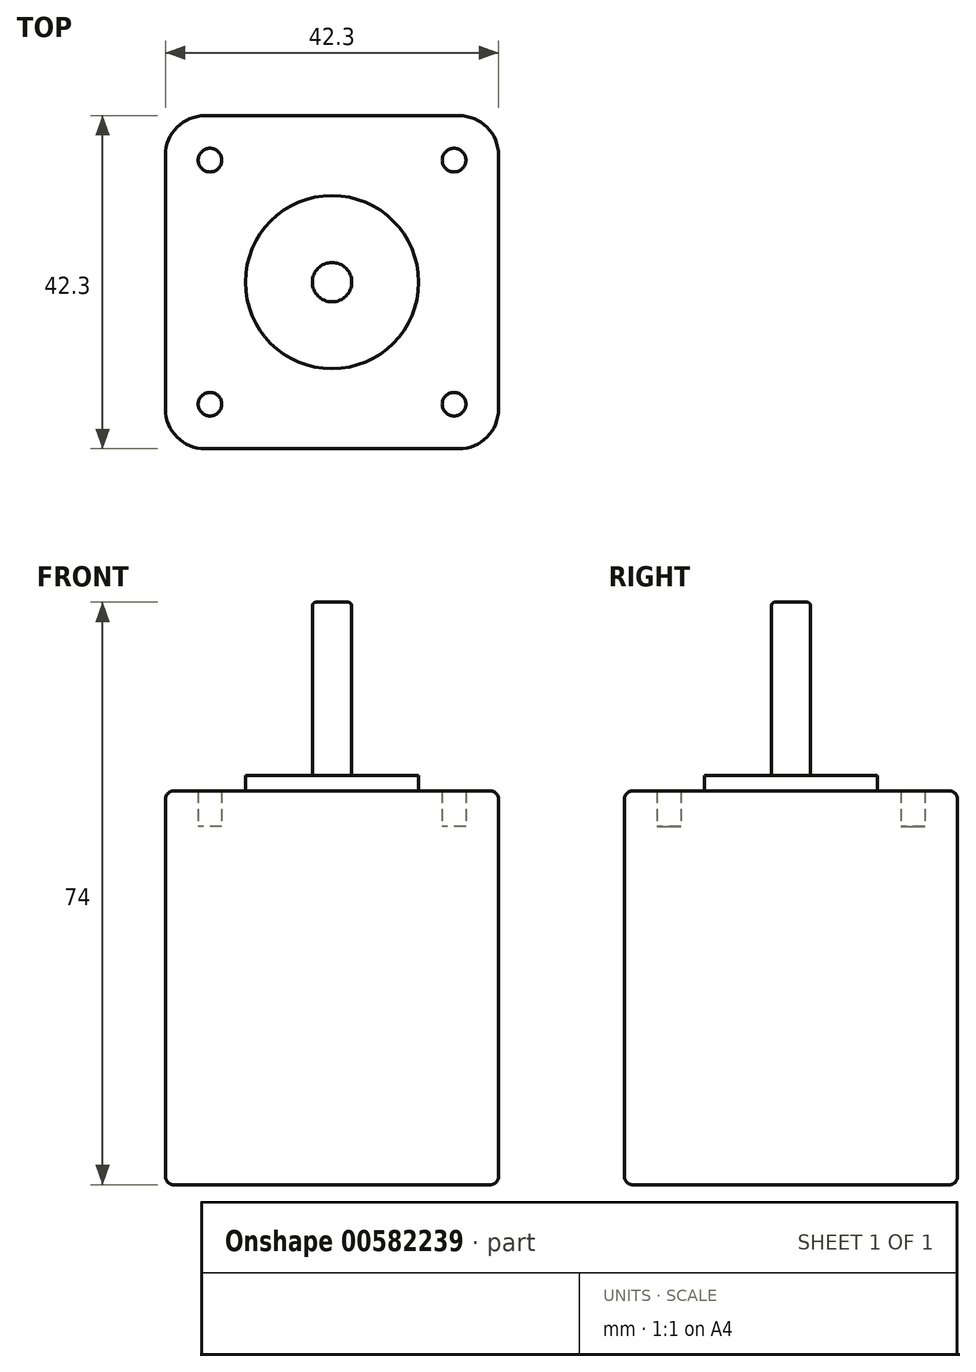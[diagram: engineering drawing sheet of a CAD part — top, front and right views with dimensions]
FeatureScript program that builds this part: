
annotation { "Feature Type Name" : "Feature", "Feature Type Description" : "" }
export const myFeature = defineFeature(function(context is Context, id is Id, definition is map)
    precondition{}
    {
        {
            assignVariable(context, id + "F0", {"name" : "Height", "anyValue" : 50});
        }
        {
            var Q0;
            Q0=qCreatedBy(makeId("Top.planeOp"),FACE);
            var sketch = newSketch(context, id + "F1", { "sketchPlane" : qUnion([Q0])});
            skLineSegment(sketch, "E0.bottom", {"start": v(-21.15, 21.15) * mm, "end": v(21.15, 21.15) * mm});
            skLineSegment(sketch, "E0.top", {"start": v(-21.15, -21.15) * mm, "end": v(21.15, -21.15) * mm});
            skLineSegment(sketch, "E0.left", {"start": v(-21.15, 21.15) * mm, "end": v(-21.15, -21.15) * mm});
            skLineSegment(sketch, "E0.right", {"start": v(21.15, 21.15) * mm, "end": v(21.15, -21.15) * mm});
            skLineSegment(sketch, "E1.bottom", {"start": v(-15.5, 15.5) * mm, "end": v(15.5, 15.5) * mm, "construction": true});
            skLineSegment(sketch, "E1.top", {"start": v(-15.5, -15.5) * mm, "end": v(15.5, -15.5) * mm, "construction": true});
            skLineSegment(sketch, "E1.left", {"start": v(-15.5, 15.5) * mm, "end": v(-15.5, -15.5) * mm, "construction": true});
            skLineSegment(sketch, "E1.right", {"start": v(15.5, 15.5) * mm, "end": v(15.5, -15.5) * mm, "construction": true});
            skCircle(sketch, "E2", {"center": v(-15.5, 15.5) * mm, "radius": 1.5 * mm});
            skCircle(sketch, "E3", {"center": v(15.5, 15.5) * mm, "radius": 1.5 * mm});
            skCircle(sketch, "E4", {"center": v(15.5, -15.5) * mm, "radius": 1.5 * mm});
            skCircle(sketch, "E5", {"center": v(-15.5, -15.5) * mm, "radius": 1.5 * mm});
            skCircle(sketch, "E6", {"center": v(0, 0) * mm, "radius": 11 * mm});
            skCircle(sketch, "E7", {"center": v(0, 0) * mm, "radius": 2.5 * mm});
            skSolve(sketch);
        }
        {
            var Q0;
            Q0=makeQuery(id+"F1.imprint","IMPRINT",FACE,{"disambiguationData":[TD([[makeQuery(id+"F1.imprint","IMPRINT",EDGE,{"derivedFrom":sQuery(id+"F1.wireOp",EDGE,"E2")}),1.0]])]});
            var Q1;
            Q1=makeQuery(id+"F1.imprint","IMPRINT",FACE,{"disambiguationData":[TD([[makeQuery(id+"F1.imprint","IMPRINT",EDGE,{"derivedFrom":sQuery(id+"F1.wireOp",EDGE,"E5")}),1.0]])]});
            var Q2;
            Q2=makeQuery(id+"F1.imprint","IMPRINT",FACE,{"disambiguationData":[TD([[makeQuery(id+"F1.imprint","IMPRINT",EDGE,{"derivedFrom":sQuery(id+"F1.wireOp",EDGE,"E4")}),1.0]])]});
            var Q3;
            Q3=makeQuery(id+"F1.imprint","IMPRINT",FACE,{"disambiguationData":[TD([[makeQuery(id+"F1.imprint","IMPRINT",EDGE,{"derivedFrom":sQuery(id+"F1.wireOp",EDGE,"E3")}),1.0]])]});
            var Q4;
            Q4=makeQuery(id+"F1.imprint","IMPRINT",FACE,{"disambiguationData":[TD([[makeQuery(id+"F1.imprint","IMPRINT",EDGE,{"derivedFrom":sQuery(id+"F1.wireOp",EDGE,"E0.bottom")}),-1.0]])]});
            var Q5;
            Q5=makeQuery(id+"F1.imprint","IMPRINT",FACE,{"disambiguationData":[TD([[makeQuery(id+"F1.imprint","IMPRINT",EDGE,{"derivedFrom":sQuery(id+"F1.wireOp",EDGE,"E6")}),1.0]])]});
            var Q6;
            Q6=makeQuery(id+"F1.imprint","IMPRINT",FACE,{"disambiguationData":[TD([[makeQuery(id+"F1.imprint","IMPRINT",EDGE,{"derivedFrom":sQuery(id+"F1.wireOp",EDGE,"E7")}),1.0]])]});
            extrude(context, id + "F2", {"entities" : qUnion([Q0, Q1, Q2, Q3, Q4, Q5, Q6]), "depth" : (getVariable(context, 'Height') - 4.5) * mm, "offsetDistance" : 25 * mm});
        }
        {
            var Q0;
            Q0=makeQuery(id+"F1.imprint","IMPRINT",FACE,{"disambiguationData":[TD([[makeQuery(id+"F1.imprint","IMPRINT",EDGE,{"derivedFrom":sQuery(id+"F1.wireOp",EDGE,"E0.bottom")}),-1.0]])]});
            var Q1;
            Q1=makeQuery(id+"F1.imprint","IMPRINT",FACE,{"disambiguationData":[TD([[makeQuery(id+"F1.imprint","IMPRINT",EDGE,{"derivedFrom":sQuery(id+"F1.wireOp",EDGE,"E6")}),1.0]])]});
            var Q2;
            Q2=makeQuery(id+"F1.imprint","IMPRINT",FACE,{"disambiguationData":[TD([[makeQuery(id+"F1.imprint","IMPRINT",EDGE,{"derivedFrom":sQuery(id+"F1.wireOp",EDGE,"E7")}),1.0]])]});
            extrude(context, id + "F3", {"entities" : qUnion([Q0, Q1, Q2]), "operationType" : NewBodyOperationType.ADD, "depth" : (getVariable(context, 'Height')) * mm, "offsetDistance" : 25 * mm, "hasSecondDirection" : true, "secondDirectionOppositeDirection" : false, "secondDirectionDepth" : (getVariable(context, 'Height') - 4.5) * mm});
        }
        {
            var Q0;
            Q0=makeQuery(id+"F1.imprint","IMPRINT",FACE,{"disambiguationData":[TD([[makeQuery(id+"F1.imprint","IMPRINT",EDGE,{"derivedFrom":sQuery(id+"F1.wireOp",EDGE,"E6")}),1.0]])]});
            var Q1;
            Q1=makeQuery(id+"F1.imprint","IMPRINT",FACE,{"disambiguationData":[TD([[makeQuery(id+"F1.imprint","IMPRINT",EDGE,{"derivedFrom":sQuery(id+"F1.wireOp",EDGE,"E7")}),1.0]])]});
            extrude(context, id + "F4", {"entities" : qUnion([Q0, Q1]), "operationType" : NewBodyOperationType.ADD, "depth" : (getVariable(context, 'Height') + 2) * mm, "offsetDistance" : 25 * mm, "hasSecondDirection" : true, "secondDirectionOppositeDirection" : false, "secondDirectionDepth" : (getVariable(context, 'Height')) * mm});
        }
        {
            var Q0;
            Q0=makeQuery(id+"F1.imprint","IMPRINT",FACE,{"disambiguationData":[TD([[makeQuery(id+"F1.imprint","IMPRINT",EDGE,{"derivedFrom":sQuery(id+"F1.wireOp",EDGE,"E7")}),1.0]])]});
            extrude(context, id + "F5", {"entities" : qUnion([Q0]), "operationType" : NewBodyOperationType.ADD, "depth" : (getVariable(context, 'Height') + 24) * mm, "offsetDistance" : 25 * mm, "hasSecondDirection" : true, "secondDirectionOppositeDirection" : false, "secondDirectionDepth" : (getVariable(context, 'Height') + 2) * mm});
        }
        {
            var Q0;
            Q0=makeQuery(id+"F5.opExtrude","CAP_EDGE",EDGE,{"disambiguationData":[OSD([sQuery(id+"F1.wireOp",EDGE,"E7")])],"isStart":false});
            fillet(context, id + "F6", {"entities" : qUnion([Q0]), "radius" : 0.5 * mm, "tangentPropagation" : true, "allowEdgeOverflow" : false});
        }
        {
            var Q0;
            {var subQ0=sQuery(id+"F1.wireOp",EDGE,"E0.left");var subQ1=sQuery(id+"F1.wireOp",EDGE,"E0.top");Q0=makeQuery(id+"F3.boolean.opBoolean","MERGE",EDGE,{"derivedFrom":[makeQuery(id+"F2.opExtrude","SWEPT_EDGE",EDGE,{"disambiguationData":[OSD([subQ1,subQ0])]}),makeQuery(id+"F3.opExtrude","SWEPT_EDGE",EDGE,{"disambiguationData":[OSD([subQ1,subQ0])]})]});}
            var Q1;
            {var subQ0=sQuery(id+"F1.wireOp",EDGE,"E0.left");var subQ1=sQuery(id+"F1.wireOp",EDGE,"E0.bottom");Q1=makeQuery(id+"F3.boolean.opBoolean","MERGE",EDGE,{"derivedFrom":[makeQuery(id+"F2.opExtrude","SWEPT_EDGE",EDGE,{"disambiguationData":[OSD([subQ1,subQ0])]}),makeQuery(id+"F3.opExtrude","SWEPT_EDGE",EDGE,{"disambiguationData":[OSD([subQ1,subQ0])]})]});}
            var Q2;
            {var subQ0=sQuery(id+"F1.wireOp",EDGE,"E0.right");var subQ1=sQuery(id+"F1.wireOp",EDGE,"E0.bottom");Q2=makeQuery(id+"F3.boolean.opBoolean","MERGE",EDGE,{"derivedFrom":[makeQuery(id+"F2.opExtrude","SWEPT_EDGE",EDGE,{"disambiguationData":[OSD([subQ1,subQ0])]}),makeQuery(id+"F3.opExtrude","SWEPT_EDGE",EDGE,{"disambiguationData":[OSD([subQ1,subQ0])]})]});}
            var Q3;
            {var subQ0=sQuery(id+"F1.wireOp",EDGE,"E0.right");var subQ1=sQuery(id+"F1.wireOp",EDGE,"E0.top");Q3=makeQuery(id+"F3.boolean.opBoolean","MERGE",EDGE,{"derivedFrom":[makeQuery(id+"F2.opExtrude","SWEPT_EDGE",EDGE,{"disambiguationData":[OSD([subQ1,subQ0])]}),makeQuery(id+"F3.opExtrude","SWEPT_EDGE",EDGE,{"disambiguationData":[OSD([subQ1,subQ0])]})]});}
            fillet(context, id + "F7", {"entities" : qUnion([Q0, Q1, Q2, Q3]), "radius" : 5 * mm, "tangentPropagation" : true, "allowEdgeOverflow" : false});
        }
        {
            var Q0;
            {var subQ0=sQuery(id+"F1.wireOp",EDGE,"E0.left");var subQ1=sQuery(id+"F1.wireOp",EDGE,"E0.bottom");Q0=makeQuery(id+"F7.opFillet","BLEND_EDGE",EDGE,{"blendedFrom":[makeQuery(id+"F3.boolean.opBoolean","MERGE",EDGE,{"derivedFrom":[makeQuery(id+"F2.opExtrude","SWEPT_EDGE",EDGE,{"disambiguationData":[OSD([subQ1,subQ0])]}),makeQuery(id+"F3.opExtrude","SWEPT_EDGE",EDGE,{"disambiguationData":[OSD([subQ1,subQ0])]})]}),makeQuery(id+"F3.opExtrude","CAP_FACE",FACE,{"disambiguationData":[OSD([subQ1,sQuery(id+"F1.wireOp",EDGE,"E0.top"),subQ0,sQuery(id+"F1.wireOp",EDGE,"E0.right"),sQuery(id+"F1.wireOp",EDGE,"E2"),sQuery(id+"F1.wireOp",EDGE,"E3"),sQuery(id+"F1.wireOp",EDGE,"E4"),sQuery(id+"F1.wireOp",EDGE,"E5")])],"isStart":false})],"blendedInto":[makeQuery(id+"F3.opExtrude","CAP_FACE",FACE,{"disambiguationData":[OSD([subQ1,sQuery(id+"F1.wireOp",EDGE,"E0.top"),subQ0,sQuery(id+"F1.wireOp",EDGE,"E0.right"),sQuery(id+"F1.wireOp",EDGE,"E2"),sQuery(id+"F1.wireOp",EDGE,"E3"),sQuery(id+"F1.wireOp",EDGE,"E4"),sQuery(id+"F1.wireOp",EDGE,"E5")])],"isStart":false})]});}
            var Q1;
            Q1=makeQuery(id+"F2.opExtrude","CAP_FACE",FACE,{"disambiguationData":[OSD([sQuery(id+"F1.wireOp",EDGE,"E0.bottom"),sQuery(id+"F1.wireOp",EDGE,"E0.top"),sQuery(id+"F1.wireOp",EDGE,"E0.left"),sQuery(id+"F1.wireOp",EDGE,"E0.right")])],"isStart":true});
            fillet(context, id + "F8", {"entities" : qUnion([Q0, Q1]), "radius" : 1 * mm, "tangentPropagation" : true, "allowEdgeOverflow" : false});
        }
    });
